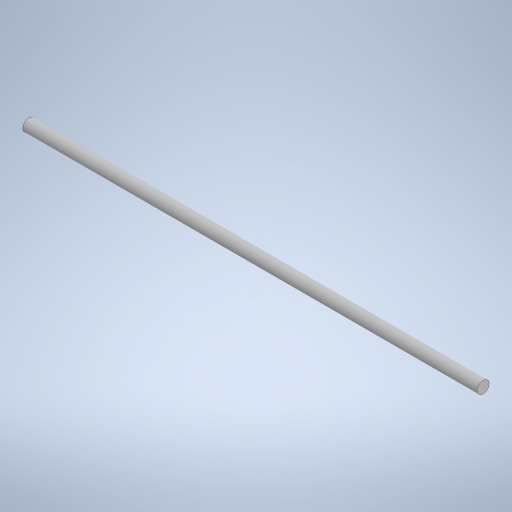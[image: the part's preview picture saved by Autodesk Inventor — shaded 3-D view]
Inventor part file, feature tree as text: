
AUTODESK INVENTOR PART (.ipt)
format: ipt  version: 2024 (Build 280153000, 153)  size: 238,592 bytes
history: native  units: in
note: dims shown in document units (in); Inventor stores cm internally (conversion verified against a paired STEP export)
features: extrude x1, sketch x1
ambient origin geometry x8: Origin, YZ Plane, XZ Plane, XY Plane, X Axis, Y Axis, Z Axis, Center Point
bodies: Solid1 (feature_tree)
feature tree (2):
  extrude  "Extrusion1"  Depth=11.75in TaperAngle=0.0deg
  sketch  "Sketch1"  dims[d0=0.315in d1=11.75in d2=0.0in]
